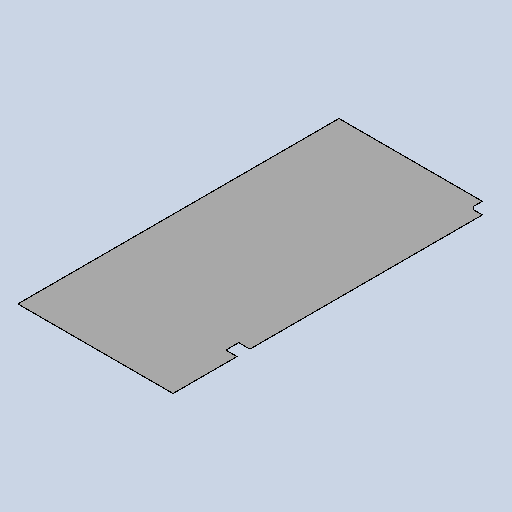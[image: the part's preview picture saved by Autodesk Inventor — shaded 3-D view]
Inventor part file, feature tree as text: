
AUTODESK INVENTOR PART (.ipt)
format: ipt  version: 2025.1 (Build 291241020, 241B)  size: 126,464 bytes
history: native  units: mm
features: other x2, sheet_metal_op x1, sketch x1
ambient origin geometry x8: Origin, YZ Plane, XZ Plane, XY Plane, X Axis, Y Axis, Z Axis, Center Point
bodies: Body1 (feature_tree)
feature tree (4):
  sheet_metal_op  "Face3"
  other  "Corner Chamfer2"
  sketch  "Sketch1"  dims[d61=500.0mm d154=1445.0mm d155=2990.0mm d156=2.0mm d159=120.0mm d161=104.0mm d162=596.0mm d163=110.0mm d164=30.0mm d165=6.0mm d166=45.0deg]
  other  "Plate5"
